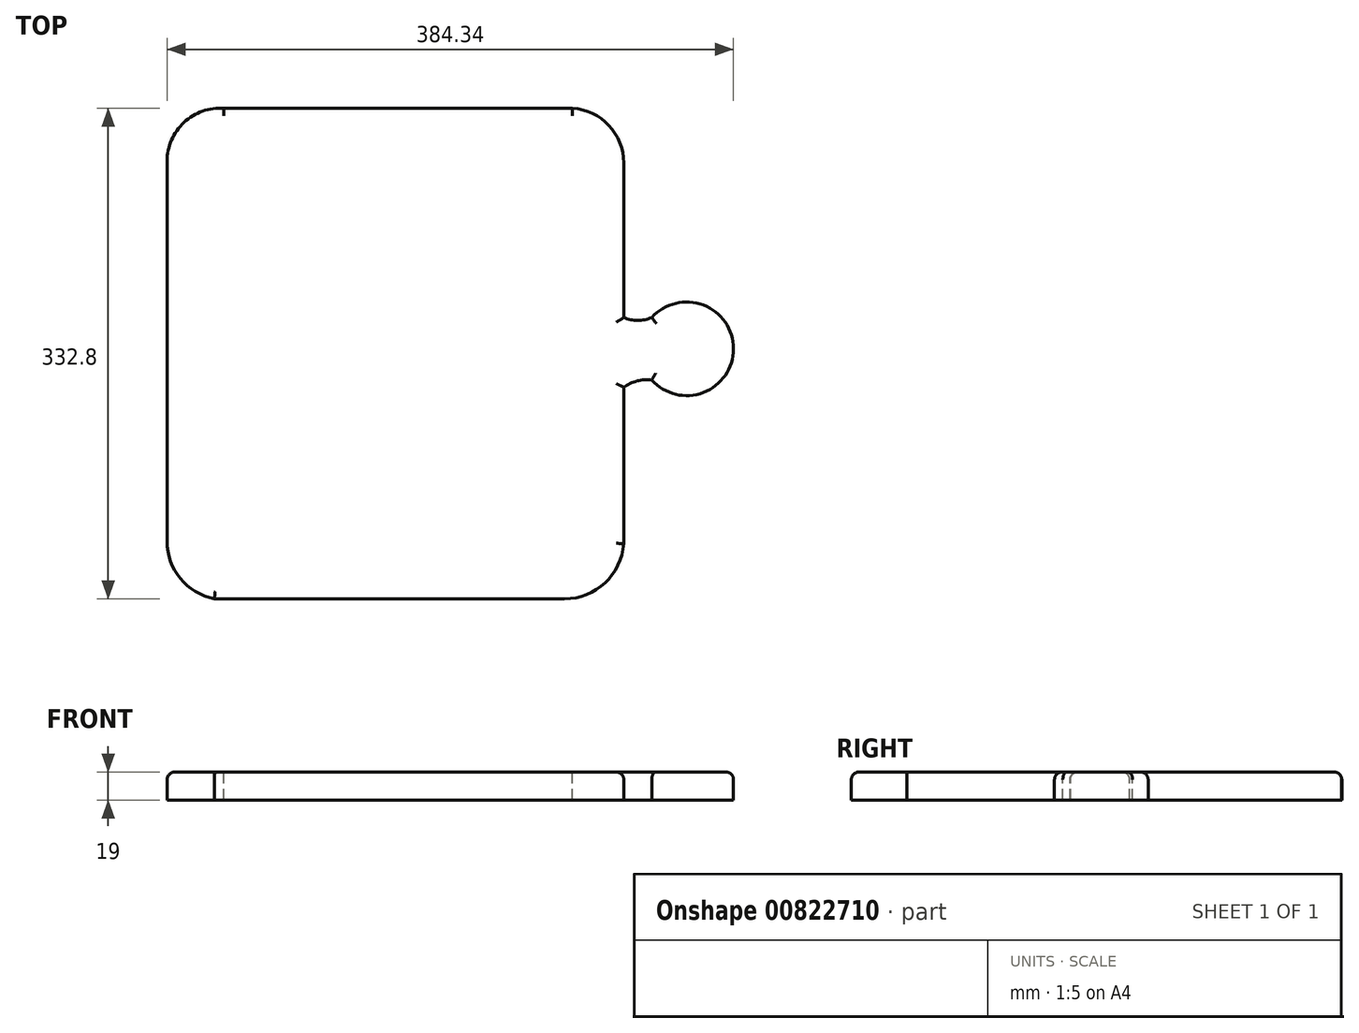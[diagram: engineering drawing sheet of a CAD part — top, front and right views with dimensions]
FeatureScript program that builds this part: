
annotation { "Feature Type Name" : "Feature", "Feature Type Description" : "" }
export const myFeature = defineFeature(function(context is Context, id is Id, definition is map)
    precondition{}
    {
        {
            var Q0;
            Q0=qCreatedBy(makeId("Top.planeOp"),FACE);
            var sketch = newSketch(context, id + "F0", { "sketchPlane" : qUnion([Q0])});
            skLineSegment(sketch, "E0.bottom", {"start": v(200, 175) * mm, "end": v(-200, 175) * mm});
            skLineSegment(sketch, "E0.top", {"start": v(200, -175) * mm, "end": v(-200, -175) * mm});
            skLineSegment(sketch, "E0.left", {"start": v(200, 175) * mm, "end": v(200, -175) * mm});
            skLineSegment(sketch, "E0.right", {"start": v(-200, 175) * mm, "end": v(-200, -175) * mm});
            skPoint(sketch, "E0.middle", {"position": v(0, 0) * mm});
            skSolve(sketch);
        }
        {
            var Q0;
            Q0 = qSketchRegion(id + "F0", true);
            extrude(context, id + "F1", {"entities" : qUnion([Q0]), "depth" : 19 * mm, "offsetDistance" : 25 * mm});
        }
        {
            var Q0;
            Q0=makeQuery(id+"F1.opExtrude","CAP_FACE",FACE,{"disambiguationData":[OSD([sQuery(id+"F0.wireOp",EDGE,"E0.bottom"),sQuery(id+"F0.wireOp",EDGE,"E0.top"),sQuery(id+"F0.wireOp",EDGE,"E0.left"),sQuery(id+"F0.wireOp",EDGE,"E0.right")])],"isStart":false});
            var sketch = newSketch(context, id + "F2", { "sketchPlane" : qUnion([Q0])});
            skLineSegment(sketch, "E1", {"start": v(-187.28, 129.66) * mm, "end": v(-187.28, -128.03) * mm});
            skArc(sketch, "E2", {"start": v(-187.28, -128.03) * mm, "mid": v(-178.24, -153.33) * mm, "end": v(-155.2, -167.17) * mm});
            skLineSegment(sketch, "E3", {"start": v(-155.2, -167.17) * mm, "end": v(82.36, -167.17) * mm});
            skArc(sketch, "E4", {"start": v(82.36, -167.17) * mm, "mid": v(109.86, -156.34) * mm, "end": v(122.6, -129.66) * mm});
            skLineSegment(sketch, "E5", {"start": v(122.6, -129.66) * mm, "end": v(122.6, -23.65) * mm});
            skArc(sketch, "E6", {"start": v(141.62, -18.76) * mm, "mid": v(131.63, -19.35) * mm, "end": v(122.6, -23.65) * mm});
            skArc(sketch, "E7", {"start": v(141.62, -18.76) * mm, "mid": v(197.06, 2.45) * mm, "end": v(141.62, 23.65) * mm});
            skArc(sketch, "E8", {"start": v(122.6, 23.65) * mm, "mid": v(132.1, 21.67) * mm, "end": v(141.62, 23.65) * mm});
            skLineSegment(sketch, "E9", {"start": v(122.6, 23.65) * mm, "end": v(122.6, 128.57) * mm});
            skArc(sketch, "E10", {"start": v(122.6, 128.57) * mm, "mid": v(112.52, 153.95) * mm, "end": v(87.8, 165.54) * mm});
            skLineSegment(sketch, "E11", {"start": v(87.8, 165.54) * mm, "end": v(-148.69, 165.54) * mm});
            skArc(sketch, "E12", {"start": v(-148.69, 165.54) * mm, "mid": v(-175.8, 156) * mm, "end": v(-187.28, 129.66) * mm});
            skSolve(sketch);
        }
        {
            var Q0;
            Q0=makeQuery(id+"F2.imprint","IMPRINT",FACE,{"disambiguationData":[TD([[makeQuery(id+"F2.imprint","IMPRINT",EDGE,{"derivedFrom":sQuery(id+"F2.wireOp",EDGE,"E1")}),-1.0]])]});
            extrude(context, id + "F3", {"entities" : qUnion([Q0]), "operationType" : NewBodyOperationType.REMOVE, "endBound" : BoundingType.THROUGH_ALL, "oppositeDirection" : true, "depth" : 25 * mm, "offsetDistance" : 25 * mm});
        }
        {
            var Q0;
            Q0=makeQuery(id+"F1.opExtrude","CAP_FACE",FACE,{"disambiguationData":[OSD([sQuery(id+"F0.wireOp",EDGE,"E0.bottom"),sQuery(id+"F0.wireOp",EDGE,"E0.top"),sQuery(id+"F0.wireOp",EDGE,"E0.left"),sQuery(id+"F0.wireOp",EDGE,"E0.right")])],"isStart":false});
            fillet(context, id + "F4", {"entities" : qUnion([Q0]), "radius" : 5 * mm, "tangentPropagation" : true, "allowEdgeOverflow" : false});
        }
    });
